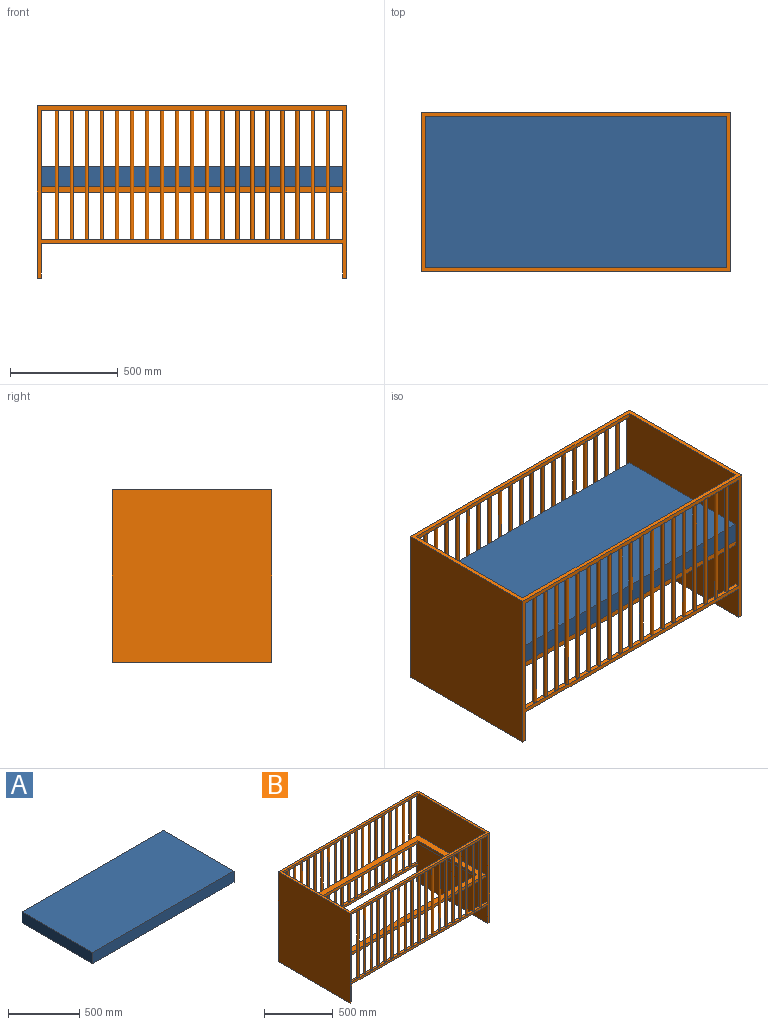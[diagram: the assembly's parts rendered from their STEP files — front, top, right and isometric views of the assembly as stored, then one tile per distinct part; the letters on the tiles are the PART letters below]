
ASSEMBLY  parts=2 mates=1
PART A: 11 faces, bbox 1400x700x120 mm
  f0: plane 600x25mm, normal (1,0,0), area 15000mm2, adj f1,f3,f4,f6
  f1: plane 1300x25mm, normal (0,1,0), area 32500mm2, adj f0,f2,f4,f6
  f2: plane 600x25mm, normal (-1,0,0), area 15000mm2, adj f1,f3,f4,f6
  f3: plane 1300x25mm, normal (0,-1,0), area 32500mm2, adj f0,f2,f4,f6
  f4: plane 1300x600mm, normal (0,0,-1), area 780000mm2, adj f0,f1,f2,f3
  f5: plane 1400x95mm, normal (0,1,0), area 133000mm2, adj f6,f7,f8,f10
  f6: plane 1400x700mm, normal (0,0,-1), area 200000mm2, adj f0,f1,f2,f3,f5,f7,f8,f9
  f7: plane 700x95mm, normal (-1,0,0), area 66500mm2, adj f5,f6,f9,f10
  f8: plane 700x95mm, normal (1,0,0), area 66500mm2, adj f5,f6,f9,f10
  f9: plane 1400x95mm, normal (0,-1,0), area 133000mm2, adj f6,f7,f8,f10
  f10: plane 1400x700mm, normal (0,0,1), area 980000mm2, adj f5,f7,f8,f9
PART B: 65 faces, bbox 1440x740x800 mm
  f0: plane 800x740mm, normal (1,0,0), area 572900mm2, adj f2,f7,f8,f9,f10,f12,f13,f14
  f1: plane 800x740mm, normal (-1,0,0), area 572900mm2, adj f2,f7,f8,f9,f10,f12,f14,f16
  f2: plane 1400x25mm, normal (0,1,0), area 35000mm2, adj f0,f1,f8,f9
  f3: plane 1300x25mm, normal (0,-1,0), area 32500mm2, adj f4,f6,f8,f9
  f4: plane 600x25mm, normal (-1,0,0), area 15000mm2, adj f3,f5,f8,f9
  f5: plane 1300x25mm, normal (0,1,0), area 32500mm2, adj f4,f6,f8,f9
  f6: plane 600x25mm, normal (1,0,0), area 15000mm2, adj f3,f5,f8,f9
  f7: plane 1400x25mm, normal (0,-1,0), area 35000mm2, adj f0,f1,f8,f9
  f8: plane 1400x700mm, normal (0,0,1), area 200000mm2, adj f0,f1,f2,f3,f4,f5,f6,f7
  f9: plane 1400x700mm, normal (0,0,-1), area 200000mm2, adj f0,f1,f2,f3,f4,f5,f6,f7
  f10: plane 1440x800mm, normal (0,-1,0), area 88000mm2, adj f0,f1,f11,f13,f14,f15,f16,f18
  f11: plane 800x740mm, normal (-1,0,0), area 592000mm2, adj f10,f12,f13,f14
  f12: plane 1440x800mm, normal (0,1,0), area 88000mm2, adj f0,f1,f11,f13,f14,f15,f16,f20
  f13: plane 740x20mm, normal (0,0,-1), area 14800mm2, adj f0,f10,f11,f12
  f14: plane 1440x740mm, normal (0,0,1), area 85600mm2, adj f0,f1,f10,f11,f12,f15,f17,f19
  f15: plane 800x740mm, normal (1,0,0), area 592000mm2, adj f10,f12,f14,f16
  f16: plane 740x20mm, normal (0,0,-1), area 14800mm2, adj f1,f10,f12,f15
  f17: plane 1400x20mm, normal (0,1,0), area 28000mm2, adj f0,f1,f14,f18
  f18: plane 1400x20mm, normal (0,0,-1), area 23165.1mm2, adj f0,f1,f10,f17,f27,f28,f29,f30
  f19: plane 1400x20mm, normal (0,-1,0), area 28000mm2, adj f0,f1,f14,f20
  f20: plane 1400x20mm, normal (0,0,-1), area 23165.1mm2, adj f0,f1,f12,f19,f46,f47,f48,f49
  f21: plane 1400x20mm, normal (0,0,-1), area 28000mm2, adj f0,f1,f10,f22
  f22: plane 1400x20mm, normal (0,1,0), area 28000mm2, adj f0,f1,f21,f23
  f23: plane 1400x20mm, normal (0,0,1), area 23165.1mm2, adj f0,f1,f10,f22,f27,f28,f29,f30
  f24: plane 1400x20mm, normal (0,-1,0), area 28000mm2, adj f0,f1,f25,f26
  f25: plane 1400x20mm, normal (0,0,-1), area 28000mm2, adj f0,f1,f12,f24
  f26: plane 1400x20mm, normal (0,0,1), area 23165.1mm2, adj f0,f1,f12,f24,f46,f47,f48,f49
  f27: cylinder r=9mm len=600mm, axis (0,0,-1), area 33929.2mm2, adj f18,f23
  f28: cylinder r=9mm len=600mm, axis (0,0,-1), area 33929.2mm2, adj f18,f23
  f29: cylinder r=9mm len=600mm, axis (0,0,-1), area 33929.2mm2, adj f18,f23
  f30: cylinder r=9mm len=600mm, axis (0,0,-1), area 33929.2mm2, adj f18,f23
  f31: cylinder r=9mm len=600mm, axis (0,0,-1), area 33929.2mm2, adj f18,f23
  f32: cylinder r=9mm len=600mm, axis (0,0,-1), area 33929.2mm2, adj f18,f23
  f33: cylinder r=9mm len=600mm, axis (0,0,-1), area 33929.2mm2, adj f18,f23
  f34: cylinder r=9mm len=600mm, axis (0,0,-1), area 33929.2mm2, adj f18,f23
  f35: cylinder r=9mm len=600mm, axis (0,0,-1), area 33929.2mm2, adj f18,f23
  f36: cylinder r=9mm len=600mm, axis (0,0,-1), area 33929.2mm2, adj f18,f23
  f37: cylinder r=9mm len=600mm, axis (0,0,-1), area 33929.2mm2, adj f18,f23
  f38: cylinder r=9mm len=600mm, axis (0,0,-1), area 33929.2mm2, adj f18,f23
  f39: cylinder r=9mm len=600mm, axis (0,0,-1), area 33929.2mm2, adj f18,f23
  f40: cylinder r=9mm len=600mm, axis (0,0,-1), area 33929.2mm2, adj f18,f23
  f41: cylinder r=9mm len=600mm, axis (0,0,-1), area 33929.2mm2, adj f18,f23
  f42: cylinder r=9mm len=600mm, axis (0,0,-1), area 33929.2mm2, adj f18,f23
  f43: cylinder r=9mm len=600mm, axis (0,0,-1), area 33929.2mm2, adj f18,f23
  f44: cylinder r=9mm len=600mm, axis (0,0,-1), area 33929.2mm2, adj f18,f23
  f45: cylinder r=9mm len=600mm, axis (0,0,-1), area 33929.2mm2, adj f18,f23
  f46: cylinder r=9mm len=600mm, axis (0,0,-1), area 33929.2mm2, adj f20,f26
  f47: cylinder r=9mm len=600mm, axis (0,0,-1), area 33929.2mm2, adj f20,f26
  f48: cylinder r=9mm len=600mm, axis (0,0,-1), area 33929.2mm2, adj f20,f26
  f49: cylinder r=9mm len=600mm, axis (0,0,-1), area 33929.2mm2, adj f20,f26
  f50: cylinder r=9mm len=600mm, axis (0,0,-1), area 33929.2mm2, adj f20,f26
  f51: cylinder r=9mm len=600mm, axis (0,0,-1), area 33929.2mm2, adj f20,f26
  f52: cylinder r=9mm len=600mm, axis (0,0,-1), area 33929.2mm2, adj f20,f26
  f53: cylinder r=9mm len=600mm, axis (0,0,-1), area 33929.2mm2, adj f20,f26
  f54: cylinder r=9mm len=600mm, axis (0,0,-1), area 33929.2mm2, adj f20,f26
  f55: cylinder r=9mm len=600mm, axis (0,0,-1), area 33929.2mm2, adj f20,f26
  f56: cylinder r=9mm len=600mm, axis (0,0,-1), area 33929.2mm2, adj f20,f26
  f57: cylinder r=9mm len=600mm, axis (0,0,-1), area 33929.2mm2, adj f20,f26
  f58: cylinder r=9mm len=600mm, axis (0,0,-1), area 33929.2mm2, adj f20,f26
  f59: cylinder r=9mm len=600mm, axis (0,0,-1), area 33929.2mm2, adj f20,f26
  f60: cylinder r=9mm len=600mm, axis (0,0,-1), area 33929.2mm2, adj f20,f26
  f61: cylinder r=9mm len=600mm, axis (0,0,-1), area 33929.2mm2, adj f20,f26
  f62: cylinder r=9mm len=600mm, axis (0,0,-1), area 33929.2mm2, adj f20,f26
  f63: cylinder r=9mm len=600mm, axis (0,0,-1), area 33929.2mm2, adj f20,f26
  f64: cylinder r=9mm len=600mm, axis (0,0,-1), area 33929.2mm2, adj f20,f26
PLACE A at identity
PLACE B at identity fixed
MATE fastened B.f8 <-> A.f6  axis (0,0,1) through (-700,-350,25)mm
